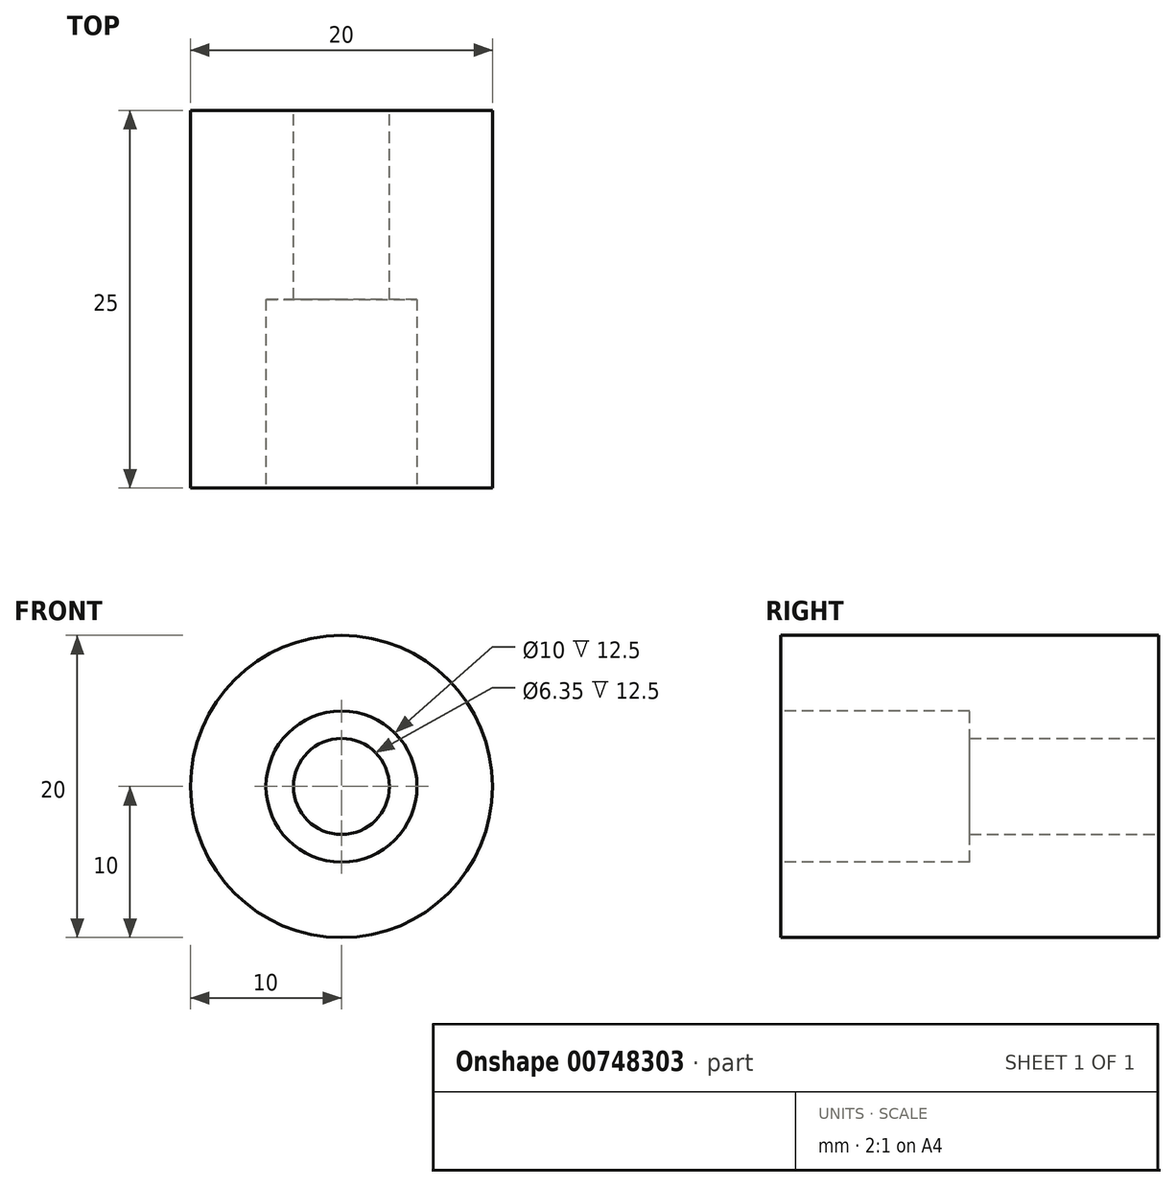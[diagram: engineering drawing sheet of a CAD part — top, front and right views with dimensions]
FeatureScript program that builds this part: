
annotation { "Feature Type Name" : "Feature", "Feature Type Description" : "" }
export const myFeature = defineFeature(function(context is Context, id is Id, definition is map)
    precondition{}
    {
        {
            var Q0;
            Q0=qCreatedBy(makeId("Front.planeOp"),FACE);
            var sketch = newSketch(context, id + "F0", { "sketchPlane" : qUnion([Q0])});
            skCircle(sketch, "E0", {"center": v(0, 0) * mm, "radius": 10 * mm});
            skSolve(sketch);
        }
        {
            var Q0;
            Q0 = qSketchRegion(id + "F0", true);
            extrude(context, id + "F1", {"entities" : qUnion([Q0]), "depth" : 25 * mm, "offsetDistance" : 25.4 * mm});
        }
        {
            var Q0;
            Q0=makeQuery(id+"F1.opExtrude","CAP_FACE",FACE,{"disambiguationData":[OSD([sQuery(id+"F0.wireOp",EDGE,"E0")])],"isStart":false});
            var sketch = newSketch(context, id + "F2", { "sketchPlane" : qUnion([Q0])});
            skCircle(sketch, "E1", {"center": v(0, 0) * mm, "radius": 5 * mm});
            skSolve(sketch);
        }
        {
            var Q0;
            Q0 = qSketchRegion(id + "F2", true);
            extrude(context, id + "F3", {"entities" : qUnion([Q0]), "operationType" : NewBodyOperationType.REMOVE, "oppositeDirection" : true, "depth" : 12.5 * mm, "offsetDistance" : 25.4 * mm});
        }
        {
            var Q0;
            Q0=makeQuery(id+"F1.opExtrude","CAP_FACE",FACE,{"disambiguationData":[OSD([sQuery(id+"F0.wireOp",EDGE,"E0")])],"isStart":true});
            var sketch = newSketch(context, id + "F4", { "sketchPlane" : qUnion([Q0])});
            skCircle(sketch, "E2", {"center": v(0, 0) * mm, "radius": 3.17 * mm});
            skSolve(sketch);
        }
        {
            var Q0;
            Q0 = qSketchRegion(id + "F4", true);
            extrude(context, id + "F5", {"entities" : qUnion([Q0]), "operationType" : NewBodyOperationType.REMOVE, "endBound" : BoundingType.THROUGH_ALL, "oppositeDirection" : true, "depth" : 25.4 * mm, "offsetDistance" : 25.4 * mm});
        }
    });
